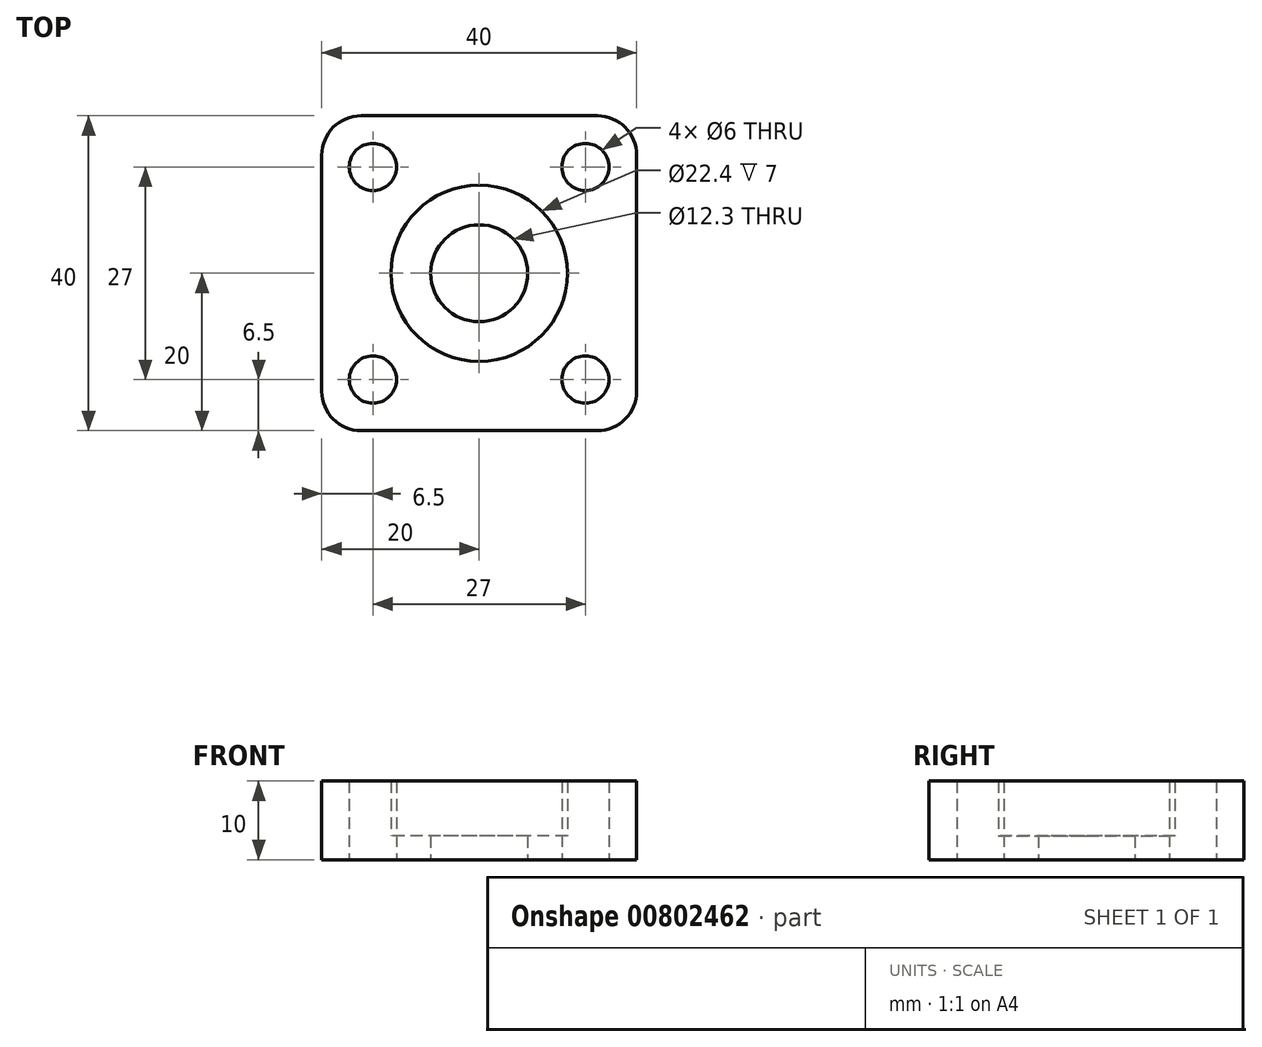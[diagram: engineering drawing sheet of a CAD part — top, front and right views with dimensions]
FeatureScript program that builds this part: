
annotation { "Feature Type Name" : "Feature", "Feature Type Description" : "" }
export const myFeature = defineFeature(function(context is Context, id is Id, definition is map)
    precondition{}
    {
        {
            var Q0;
            Q0=qCreatedBy(makeId("Top.planeOp"),FACE);
            var sketch = newSketch(context, id + "F0", { "sketchPlane" : qUnion([Q0])});
            skCircle(sketch, "E0", {"center": v(0, 0) * mm, "radius": 11.2 * mm});
            skCircle(sketch, "E1", {"center": v(0, 0) * mm, "radius": 6.15 * mm});
            skLineSegment(sketch, "E2.bottom", {"start": v(20, -20) * mm, "end": v(-20, -20) * mm});
            skLineSegment(sketch, "E2.top", {"start": v(20, 20) * mm, "end": v(-20, 20) * mm});
            skLineSegment(sketch, "E2.left", {"start": v(20, -20) * mm, "end": v(20, 20) * mm});
            skLineSegment(sketch, "E2.right", {"start": v(-20, -20) * mm, "end": v(-20, 20) * mm});
            skLineSegment(sketch, "E3.bottom", {"start": v(13.5, -13.5) * mm, "end": v(-13.5, -13.5) * mm, "construction": true});
            skLineSegment(sketch, "E3.top", {"start": v(13.5, 13.5) * mm, "end": v(-13.5, 13.5) * mm, "construction": true});
            skLineSegment(sketch, "E3.left", {"start": v(13.5, -13.5) * mm, "end": v(13.5, 13.5) * mm, "construction": true});
            skLineSegment(sketch, "E3.right", {"start": v(-13.5, -13.5) * mm, "end": v(-13.5, 13.5) * mm, "construction": true});
            skCircle(sketch, "E4", {"center": v(-13.5, 13.5) * mm, "radius": 3 * mm});
            skCircle(sketch, "E5", {"center": v(-13.5, -13.5) * mm, "radius": 3 * mm});
            skCircle(sketch, "E6", {"center": v(13.5, 13.5) * mm, "radius": 3 * mm});
            skCircle(sketch, "E7", {"center": v(13.5, -13.5) * mm, "radius": 3 * mm});
            skSolve(sketch);
        }
        {
            var Q0;
            Q0=makeQuery(id+"F0.imprint","IMPRINT",FACE,{"disambiguationData":[TD([[makeQuery(id+"F0.imprint","IMPRINT",EDGE,{"derivedFrom":sQuery(id+"F0.wireOp",EDGE,"E0")}),-1.0]])]});
            extrude(context, id + "F1", {"entities" : qUnion([Q0]), "depth" : 10 * mm, "offsetDistance" : 25 * mm});
        }
        {
            var Q0;
            Q0=makeQuery(id+"F0.imprint","IMPRINT",FACE,{"disambiguationData":[TD([[makeQuery(id+"F0.imprint","IMPRINT",EDGE,{"derivedFrom":sQuery(id+"F0.wireOp",EDGE,"E0")}),1.0]])]});
            extrude(context, id + "F2", {"entities" : qUnion([Q0]), "operationType" : NewBodyOperationType.ADD, "depth" : 3 * mm, "offsetDistance" : 25 * mm});
        }
        {
            var Q0;
            Q0=makeQuery(id+"F1.opExtrude","SWEPT_EDGE",EDGE,{"disambiguationData":[OSD([sQuery(id+"F0.wireOp",EDGE,"E2.bottom"),sQuery(id+"F0.wireOp",EDGE,"E2.right")])]});
            var Q1;
            Q1=makeQuery(id+"F1.opExtrude","SWEPT_EDGE",EDGE,{"disambiguationData":[OSD([sQuery(id+"F0.wireOp",EDGE,"E2.bottom"),sQuery(id+"F0.wireOp",EDGE,"E2.left")])]});
            var Q2;
            Q2=makeQuery(id+"F1.opExtrude","SWEPT_EDGE",EDGE,{"disambiguationData":[OSD([sQuery(id+"F0.wireOp",EDGE,"E2.top"),sQuery(id+"F0.wireOp",EDGE,"E2.left")])]});
            var Q3;
            Q3=makeQuery(id+"F1.opExtrude","SWEPT_EDGE",EDGE,{"disambiguationData":[OSD([sQuery(id+"F0.wireOp",EDGE,"E2.top"),sQuery(id+"F0.wireOp",EDGE,"E2.right")])]});
            fillet(context, id + "F3", {"entities" : qUnion([Q0, Q1, Q2, Q3]), "radius" : 5 * mm, "tangentPropagation" : true, "allowEdgeOverflow" : false});
        }
    });
